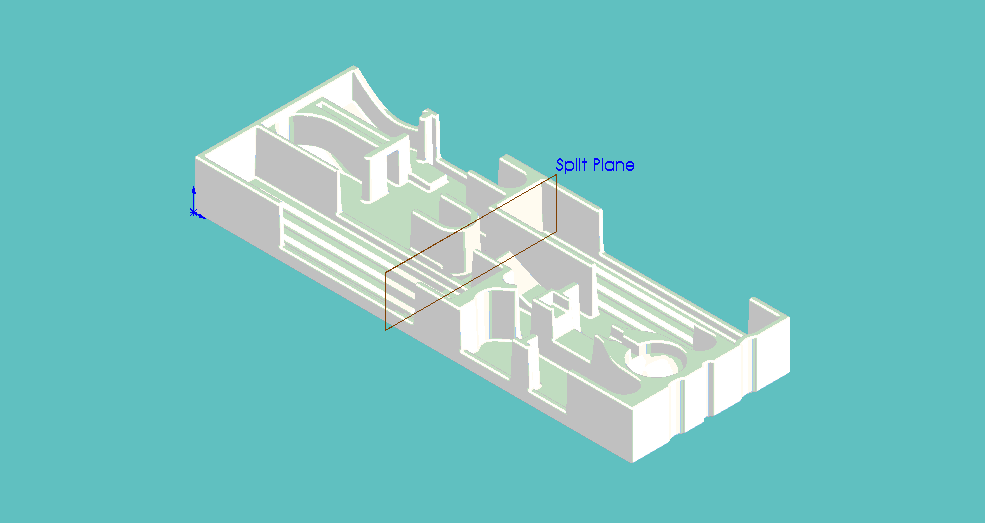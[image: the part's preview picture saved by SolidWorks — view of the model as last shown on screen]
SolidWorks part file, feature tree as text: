
SOLIDWORKS PART (.sldprt)
format: sldprt  version: not decoded by parser v0  size: 9,712,640 bytes
history: native  units: mm
features: sketch x41, fillet x24, extrude x21, cut_extrude x11, plane x9, cut_revolve x2, material x1, surface_op x1, pattern_linear x1, shell x1 + 3 further entries (+12 scaffold rows collapsed)
feature tree (127):
  "Annotations"  RD1=9.652mm RD2=4.826mm RD3=9.652mm RD4=88.988456mm RD5=139.7mm
  scaffold x12  (default folders/planes/origin — collapsed)
  material  "ABS"
  sketch  "Sketch1"  dims[c1.D1=444.5mm c1.D2=162.052mm c1.D3=73.66mm c1.D4=38.1mm c1.D5=34.798mm c1.D6=9.525mm c1.D7=54.102mm c1.D8=50.8mm c1.D9=12.7mm c1.D10=78.867mm c1.D11=444.5mm c1.D12=~5.134565mm c2.D10=~116.663513deg c2.D9=~116.663513deg]
  extrude  "Base"  Depth=5.334mm
  plane  "Split Plane"  Offset=200.66mm
  sketch  "Sketch2"
  sketch  "Sketch1<2>"  dims[D1=12.7mm D5=5.842mm D6=1.0mm D7=5.0mm]
  sketch  "Main Fork Silhouette"  dims[c1.D13=~4.796351mm c1.D1=25.4mm c1.D2=22.86mm c1.D3=50.8mm c1.D4=~12.764099mm c1.D5=~4.295901mm c1.D6=10.16mm c1.D7=17.22mm c1.D8=6.35mm c1.D9=~4.796351mm c1.D10=8.636mm c1.D11=~2.781901mm c1.D12=19.05mm c2.D13=7.874mm c2.D14=14.986mm c2.D15=1.27mm c2.D16=~5.694099mm c3.D13=12.7mm c3.D14=64.77mm c3.D15=127.0mm c3.D16=190.5mm c3.D17=76.2mm c4.D15=25.4mm c4.D13=25.4mm c4.D14=65.278mm c4.D5=69.85mm c5.D14=~69.689317mm c5.D5=~64.267148mm c6.D14=67.31mm c6.D15=~190.509647mm c6.D13=~190.509647mm c6.D4=190.5mm c6.D5=76.2mm c6.D10=25.4mm c6.D11=76.2mm]
  sketch  "Sketch43"  dims[c1.D1=444.5mm c1.D2=162.052mm c1.D3=73.66mm c1.D4=38.1mm c1.D5=34.798mm c1.D6=9.525mm c1.D7=54.102mm c1.D8=50.8mm c1.D9=12.7mm c1.D10=78.867mm c1.D11=444.5mm c1.D12=~5.134565mm c1.D13=12.7mm c1.D14=444.5mm c2.D10=~116.663513deg c2.D9=~116.663513deg]
  plane  "Plane4"
  plane  "Forky Orthogonal"
  sketch  "Sketch4"  dims[c1.D1=17.78mm c1.D2=50.8mm c1.D3=76.2mm c1.D4=190.5mm c1.D5=5.588mm c1.D6=25.4mm c2.D2=76.2mm c2.D1=19.05mm c2.D7=165.1mm c2.D3=25.4mm c2.D4=12.7mm c2.D8=~21.061514mm c3.D1=19.05mm c3.D8=~21.061514mm c3.D9=~6.917089mm c3.D10=7.62mm c3.D11=19.05mm c4.D9=6.35mm c4.D10=~196.151132mm c4.D12=1.27mm c4.D1=190.5mm c4.D2=88.9mm c4.D3=114.3mm c4.D4=165.1mm c4.D5=177.8mm c4.D6=~8.68996mm c4.D7=~3.773089mm c4.D8=~23.39312mm c5.D9=~24.468972mm c5.D10=~3.749363mm c5.D11=1.27mm]
  surface_op  "Surface-Extrude3"
  sketch  "Sketch6"  dims[c1.D1=~4.796351mm c1.D2=12.7mm c1.D3=25.4mm c1.D4=9.398mm c1.D5=~114.324562mm c1.D6=~17.167965mm c1.D7=~19.034214mm c1.D8=33.02mm c1.D9=~25.314243mm c1.D10=~25.314243mm c1.D11=~5.608325mm c1.D12=12.7mm c2.D2=~17.065791mm c2.D3=33.02mm c2.D5=8.89mm c2.D7=41.402mm c2.D9=~11.627243mm c3.D2=~23.728503mm c3.D3=33.02mm c3.D9=8.89mm c3.D10=~114.324562mm c3.D11=27.94mm c3.D12=16.51mm c3.D13=16.51mm c3.D8=29.21mm c4.D13=3.048mm c4.D3=~8.583982mm c4.D4=5.08mm c4.D6=7.62mm c4.D11=19.05mm c5.D3=~20.626017mm]
  extrude  "Border - rect - obsoleteme"  Depth=2mm
  sketch  "Sketch9"  dims[c1.D1=8.89mm c1.D2=7.62mm c1.D3=57.15mm c1.D4=88.9mm c1.D5=50.8mm c1.D6=241.3mm c2.D2=12.7mm c2.D5=50.8mm c2.D7=50.8mm c3.D5=50.8mm c3.D3=~3.85688mm c3.D7=40.64mm c3.D8=7.62mm c3.D2=~47.01887mm c4.D5=~3.296624mm c4.D4=1.27mm c4.D1=8.89mm c5.D5=~16.498931mm c5.D3=~1.019638mm c5.D2=~50.315494mm]
  extrude  "Fork Posts"  [1 undecoded]
  extrude  "Extrude Fork Support Shells Now"  [1 undecoded]
  sketch  "Sketch8"  dims[c1.D1=22.86mm c1.D2=50.8mm c1.D3=44.45mm c1.D4=19.05mm c1.D5=~4.051918mm c1.D6=12.7mm c2.D5=~196.631399mm c2.D3=2.0deg]
  sketch  "Sketch Knives"  dims[c1.D1=50.8mm c1.D2=57.15mm c1.D3=31.75mm c1.D4=7.62mm c1.D5=88.9mm c1.D6=234.95mm c2.D1=254.0mm c2.D6=57.15mm c2.D7=10.16mm c2.D5=87.376mm]
  extrude  "Extrude Knives"  Depth=44.45mm
  sketch  "Sketch32"
  extrude  "Extrude Knives Dip"  Depth=7.62mm
  sketch  "Spoon Sketch"  dims[c1.D22=~4.722235mm c1.D1=0.254mm c1.D2=25.4mm c2.D1=17.78mm c2.D2=88.9mm c2.D3=12.7mm c2.D4=21.59mm c2.D5=27.94mm c2.D6=139.7mm c2.D7=~17.102706mm c2.D8=19.05mm c3.D1=~35.769018mm c3.D9=~13.58346mm c3.D10=~5.20592mm c3.D11=~32.087876mm c3.D12=12.7mm c3.D13=8.89mm c3.D14=12.7mm c3.D15=19.05mm c3.D3=12.7mm c3.D16=19.05mm c3.D5=~2.962105mm c3.D17=~13.18974mm c3.D18=8.89mm c4.D13=12.7mm c4.D9=8.89mm c4.D11=~4.034804mm c4.D18=~17.861715mm c4.D19=~3.59156mm c4.D20=15.24mm c4.D21=11.43mm c4.D22=12.7mm c5.D21=8.89mm c5.D22=4.318mm c5.D23=2.54mm c5.D24=45.72mm c5.D25=5.842mm c6.D24=1.27mm c6.D26=2.54mm c6.D13=~8.551353mm c6.D7=35.56mm c6.D16=~10.710332mm c6.D21=~31.382311mm c6.D22=19.05mm c6.D23=17.78mm c7.D24=24.13mm c7.D27=~187.198244mm c7.D17=~4.565011mm c8.D27=~17.485259mm c8.D24=27.94mm c8.D14=~3.485167mm c8.D9=~42.034561mm c8.D20=7.62mm c8.D4=~52.413672mm c8.D21=8.636mm c9.D27=88.9mm c9.D9=1.27mm c9.D10=6.35mm c9.D11=~17.343402mm c9.D19=1.27mm c9.D6=17.78mm c9.D8=25.4mm c10.D9=~88.988456mm c10.D10=139.7mm c10.D4=~9.394223mm]
  extrude  "Extrude Chopsticks"  Depth=44.45mm
  extrude  "Measuring"  [1 undecoded]
  sketch  "Sketch12"  dims[c1.D5=12.7mm c1.D11=7.62mm c1.D1=6.35mm c1.D2=~15.116762mm c1.D3=25.4mm c1.D4=6.35mm c1.D6=~33.754585mm c2.D1=12.7mm c2.D2=6.35mm c3.D1=12.7mm c3.D3=19.05mm c3.D4=19.05mm c3.D5=6.35mm c3.D6=76.2mm c3.D7=19.05mm c3.D8=~52.225823mm c4.D5=2.54mm c4.D3=27.94mm c4.D9=2.54mm c4.D10=7.62mm c4.D11=~26.801136mm c4.D4=~16.223876mm c5.D11=~37.819224mm c5.D9=3.048mm c6.D11=8.89mm c6.D12=21.59mm c6.D13=~3.833928mm c6.D14=19.05mm c6.D7=~10.520387mm c7.D14=~3.81357mm c7.D2=127.0mm c7.D5=50.8mm c8.D2=24.13mm c8.D3=25.4mm c8.D5=20.701mm c8.D6=~17.505099mm c8.D7=38.1mm c8.D12=118.11mm c9.D5=2.54mm c9.D6=25.4mm c9.D3=20.32mm c10.D5=~64.794586mm c10.D11=~10.140817mm c10.D1=44.45mm c10.D3=2.0deg]
  extrude  "Extrude Spoon"  Depth=44.45mm
  sketch  "Sketch34"  dims[c1.D1=3.81mm c1.D2=~209.594551mm c1.D3=19.05mm c1.D4=12.7mm c1.D5=3.81mm c1.D6=3.81mm c1.D7=196.85mm c1.D8=12.7mm c1.D9=4.064mm c2.D3=13.97mm c2.D4=19.05mm c2.D9=4.064mm]
  cut_extrude  "Knife Ridges"  Depth=2.54mm
  pattern_linear  "Knife Ridges Duplicate"  Count1=3 Count2=1 Spacing1=13.97mm Spacing2=50mm
  sketch  "Spoon Base"  dims[c1.D1=~17.789559mm c1.D2=19.05mm c1.D3=8.89mm c1.D4=~17.343402mm c1.D5=22.86mm c1.D6=2.54mm c2.D4=1.778mm c2.D5=17.78mm]
  sketch  "Sketch14"  dims[c1.D1=~40.652216mm c1.D2=20.32mm c1.D3=~1.967331mm c1.D4=~2.355906mm c2.D3=13.208mm c2.D4=25.4mm c2.D5=6.604mm c2.D2=40.64mm c2.D6=~45.175591mm c2.D7=~45.175591mm c3.D6=111.76mm c3.D7=~61.957612mm c3.D1=20.32mm c3.D4=13.208mm c4.D7=6.604mm c4.D3=~3.10088mm]
  cut_extrude  "Measuring Handle"  Depth=10.16mm
  sketch  "Sketch21"  dims[D1=6.35mm D2=21.59mm D3=2.54mm]
  cut_extrude  "Measuring Hole - Obsolete"  [1 undecoded]
  plane  "Measuring Revolved"
  sketch  "Sketch29"  dims[c1.D1=~25.441103mm c1.D2=~10.394077mm c1.D3=~29.96292mm c2.D1=5.08mm c2.D2=21.59mm c2.D3=5.08mm c3.D1=3.81mm c3.D3=~22.28841mm c3.D4=17.78mm c3.D5=5.08mm c4.D3=17.78mm c4.D2=92.0deg c5.D2=~18.134795mm]
  cut_revolve  "Measuring Sphere"  Angle=360deg
  plane  "Base Plae"  Offset=2.54mm
  sketch  "Sketch30"
  cut_extrude  "Measuring Sphere Cutout"  Depth=25.4mm
  sketch  "Sketch24"  dims[c1.D1=19.05mm c1.D2=43.18mm c1.D3=~9.45227mm c1.D4=12.7mm c2.D1=~35.274667mm c2.D3=~11.282661mm c2.D4=12.7mm]
  cut_extrude  "Measuring Finger Space"  Depth=25.4mm
  sketch  "Sketch39"  dims[c1.D1=6.35mm c1.D2=6.35mm c1.D3=6.35mm c1.D4=12.7mm c1.D5=12.7mm c2.D1=16.51mm]
  extrude  "Left Wall"  Depth=5.842mm
  extrude  "Near Wall?"  Depth=44.45mm
  sketch  "Sketch15"  dims[c1.D1=19.812mm c1.D2=30.48mm c1.D3=25.4mm c1.DHA=8.89mm c2.D2=177.8mm c2.D5=15.24mm c2.D6=19.812mm c2.D7=9.652mm c2.D8=9.652mm c2.D9=4.826mm c2.D10=97.79mm c2.D11=20.32mm c2.D12=6.35mm c2.D13=177.8mm c2.D14=17.78mm c2.D15=9.652mm c2.D16=101.6mm c2.D17=13.97mm c2.D18=15.24mm c2.D19=71.12mm c2.D20=173.99mm c2.D21=177.8mm c2.D3=6.35mm c3.D5=11.43mm c3.D3=~47.801821mm c3.D13=25.4mm c3.D14=25.4mm c3.D12=41.275mm c3.D22=~3.36088mm c3.D23=38.1mm c3.D24=~10.259956mm c3.D25=~14.71477mm c3.D26=~29.42954mm c3.D19=~7.584995mm c3.D11=15.24mm c3.D17=~3.36088mm c4.D19=86.868mm c4.D4=8.89mm c4.D3=173.99mm c4.D5=20.6375mm c4.D16=~27.840044mm c4.D17=33.274mm c4.D18=~11.89112mm c5.D19=4.445mm c5.D20=10.668mm]
  extrude  "SmallFork BigSpoon Posts"  Depth=38.1mm
  extrude  "SmallFork RightPost"  [1 undecoded]
  sketch  "Sketch15<3>"  dims[D1=44.45mm D3=2.0deg]
  sketch  "Sketch46"  dims[D1=12.7mm]
  plane  "Plane10"
  sketch  "Sketch17"  dims[c1.D1=17.78mm c1.D2=40.64mm c1.D3=12.7mm c1.D4=17.78mm c2.D1=17.78mm c2.D4=6.604mm]
  "SmallFork Surface"
  sketch  "Sketch48"  dims[D1=5.08mm D2=~2.571426mm D3=25.4mm]
  "BigSpoon Surface"
  sketch  "Bigspoon Support"
  extrude  "BigSpoon Partial supp"  [1 undecoded]
  sketch  "Sketch40"  dims[c1.D2=38.1mm c1.D3=254.0mm c1.D1=35.56mm c1.D4=40.64mm c1.D5=~117.30112mm c1.D6=24.13mm c1.D7=5.842mm c1.D8=50.8mm c1.D9=~6.447221mm c1.D10=~33.117221mm c2.D1=7.62mm c2.D5=12.7mm c2.D9=~28.544759mm c2.D10=5.08mm c2.D11=38.1mm c3.D1=30.988mm]
  extrude  "Right wall"  Depth=5.842mm
  sketch  "Sketch42"
  extrude  "Far Wall"  Depth=5.842mm
  sketch  "Sketch16"  dims[c1.D1=~3.837133mm c1.D2=1.27mm c1.D3=25.4mm c2.D1=1.27mm]
  extrude  "SmallFork Support"  [1 undecoded]
  sketch  "Sketch26"  dims[c1.D1=6.35mm c1.D2=6.35mm c1.D3=11.43mm c2.D1=6.35mm c2.D2=6.35mm]
  cut_extrude  "SmallFork Ridge"  Depth=5.08mm
  sketch  "Sketch49"  dims[c1.D1=3.81mm c1.D2=3.81mm c1.D3=7.62mm c1.D4=~9.912037mm c1.D5=~30.503224mm c2.D1=3.81mm c2.D2=3.81mm c2.D3=~30.503224mm]
  cut_extrude  "Cut-Extrude1"  Depth=50.8mm
  shell  "Shell ** Shell ** Shell ** Shell"  Thickness=2.032mm
  sketch  "Split Reinforcing Sketch"  dims[D1=7.62mm]
  extrude  "Split Reinforcing"  Depth=3.81mm
  sketch  "Sketch45"  dims[c1.D1=12.7mm c1.D2=12.7mm c1.D3=20.32mm c2.D1=~10.259956mm c2.D2=~27.840044mm]
  extrude  "Extra Bigspoon Support"  Depth=24.13mm
  fillet  "Under Fillet"  Radius=1.016mm
  fillet  "Many More Fillet 0.08"  Radius=2.032mm
  sketch  "Sketch22"  dims[D1=2.54mm]
  cut_revolve  "Aborted Sphere Cutout"  Angle=360deg
  sketch  "Sketch23"  dims[D1=0.1524mm D2=0.0762mm]
  cut_extrude  "Aborted Sphere Cylinder Cut"  Depth=0.254mm
  sketch  "Sketch27"
  cut_extrude  "Aborted SmallFork Underside Rib"  Depth=8.89mm
  plane  "Plane6"
  plane  "Plane8"
  plane  "Plane9"
  sketch  "Sketch50"  dims[D1=5.08mm]
  extrude  "Measuring Shell Correction"  [1 undecoded]
  fillet  "Fillet5"  Radius=2.032mm
  fillet  "Fillet6"  Radius=2.032mm
  fillet  "Fillet7"  Radius=1.016mm
  fillet  "Fillet8"  Radius=2.032mm
  fillet  "Fillet9"  Radius=1.8288mm
  fillet  "Fillet10"  Radius=1.8288mm
  fillet  "Fillet11"  Radius=2.032mm
  fillet  "Fillet12"  Radius=1.524mm
  fillet  "Fillet14"  Radius=2.032mm
  fillet  "Fillet15"  Radius=2.032mm
  fillet  "Fillet16"  Radius=2.286mm
  fillet  "Fillet17"  Radius=1.778mm
  fillet  "Fillet18"  Radius=2.032mm
  fillet  "Fillet19"  Radius=1.778mm
  fillet  "Fillet20"  Radius=2.032mm
  fillet  "Fillet23"  Radius=0.508mm
  fillet  "Fillet24"  Radius=2.032mm
  fillet  "Fillet25"  Radius=1.016mm
  fillet  "Fillet26"  Radius=1.778mm
  fillet  "Fillet27"  Radius=2.032mm
  sketch  "Sketch51"  dims[c1.D1=2.54mm c1.D2=5.08mm c1.D3=~4.96469mm c1.D4=6.35mm c2.D3=~4.96469mm c2.D4=6.35mm]
  sketch  "Sketch20"
  cut_extrude  "Cut For Zprinter"  Depth=254mm
  cut_extrude  "Joint Holes"  Depth=5.08mm
  extrude  "Joint Studs - Suppress Me"  [1 undecoded]
  sketch  "Sketch51<2>"  dims[D1=3.81mm D3=12.0deg]
  fillet  "Joint Studs Fillet"  Radius=0.508mm
  fillet  "Joint Holes Fillet"  Radius=0.508mm
decode coverage: 85 of 102 modeling features carry decoded parameters; 3 rows unclassified (native names shown)
note: ~ marks probable driven/reference dimensions
note: 9 parameter values undecoded
summary: no parameter record found for 9 features
note: suppression state not decoded; provenance and decode notes live in map.json
